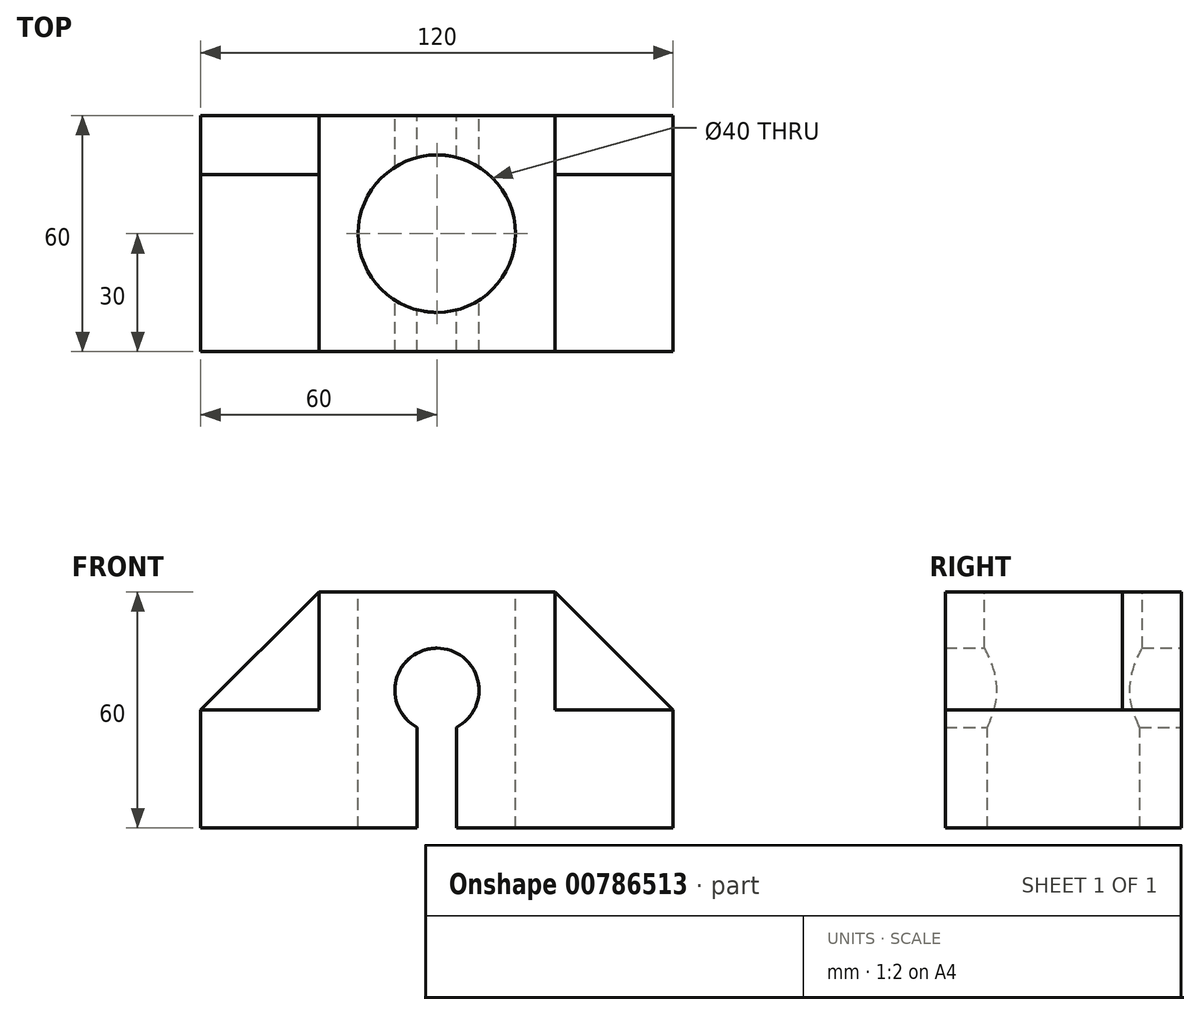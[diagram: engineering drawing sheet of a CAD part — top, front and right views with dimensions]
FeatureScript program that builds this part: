
annotation { "Feature Type Name" : "Feature", "Feature Type Description" : "" }
export const myFeature = defineFeature(function(context is Context, id is Id, definition is map)
    precondition{}
    {
        {
            var Q0;
            Q0=qCreatedBy(makeId("Front.planeOp"),FACE);
            var sketch = newSketch(context, id + "F0", { "sketchPlane" : qUnion([Q0])});
            skLineSegment(sketch, "E0.bottom", {"start": v(-60, 30) * mm, "end": v(60, 30) * mm});
            skLineSegment(sketch, "E0.top", {"start": v(-60, -30) * mm, "end": v(-5, -30) * mm});
            skLineSegment(sketch, "E0.left", {"start": v(-60, 30) * mm, "end": v(-60, -30) * mm});
            skLineSegment(sketch, "E0.right", {"start": v(60, 30) * mm, "end": v(60, -30) * mm});
            skPoint(sketch, "E0.middle", {"position": v(0, 0) * mm});
            skArc(sketch, "E1", {"start": v(5, -4.43) * mm, "mid": v(0, 15.68) * mm, "end": v(-5, -4.43) * mm});
            skLineSegment(sketch, "E2.left", {"start": v(-5, -4.43) * mm, "end": v(-5, -30) * mm});
            skLineSegment(sketch, "E2.right", {"start": v(5, -4.43) * mm, "end": v(5, -30) * mm});
            skPoint(sketch, "E2.middle", {"position": v(0, -30) * mm});
            skPoint(sketch, "E3.orphan", {"position": v(-5, 5) * mm});
            skPoint(sketch, "E4.orphan", {"position": v(5, 5) * mm});
            skPoint(sketch, "E2.top.end.orphan", {"position": v(5, -65) * mm});
            skPoint(sketch, "E2.top.start.orphan", {"position": v(-5, -65) * mm});
            skLineSegment(sketch, "E5.trimOffspring", {"start": v(5, -30) * mm, "end": v(60, -30) * mm});
            skSolve(sketch);
        }
        {
            var Q0;
            Q0=makeQuery(id+"F0.imprint","IMPRINT",FACE,{"disambiguationData":[TD([[makeQuery(id+"F0.imprint","IMPRINT",EDGE,{"derivedFrom":sQuery(id+"F0.wireOp",EDGE,"E0.bottom")}),-1.0]])]});
            extrude(context, id + "F1", {"entities" : qUnion([Q0]), "depth" : 60 * mm, "offsetDistance" : 25 * mm});
        }
        {
            var Q0;
            Q0=makeQuery(id+"F1.opExtrude","CAP_FACE",FACE,{"disambiguationData":[OSD([sQuery(id+"F0.wireOp",EDGE,"E0.bottom"),sQuery(id+"F0.wireOp",EDGE,"E0.top"),sQuery(id+"F0.wireOp",EDGE,"E0.left"),sQuery(id+"F0.wireOp",EDGE,"E0.right"),sQuery(id+"F0.wireOp",EDGE,"E1"),sQuery(id+"F0.wireOp",EDGE,"E2.left"),sQuery(id+"F0.wireOp",EDGE,"E2.right"),sQuery(id+"F0.wireOp",EDGE,"E5.trimOffspring")])],"isStart":false});
            var sketch = newSketch(context, id + "F2", { "sketchPlane" : qUnion([Q0])});
            skLineSegment(sketch, "E6.bottom", {"start": v(60, 0) * mm, "end": v(30, 0) * mm});
            skLineSegment(sketch, "E6.left", {"start": v(60, 0) * mm, "end": v(60, 30) * mm});
            skLineSegment(sketch, "E6.right", {"start": v(30, 0) * mm, "end": v(30, 30) * mm});
            skPoint(sketch, "E6.middle", {"position": v(45, 30) * mm});
            skLineSegment(sketch, "E7", {"start": v(30, 30) * mm, "end": v(60, 30) * mm});
            skPoint(sketch, "E6.top.end.orphan", {"position": v(30, 60) * mm});
            skPoint(sketch, "E8.orphan", {"position": v(60, 60) * mm});
            skLineSegment(sketch, "E9.bottom", {"start": v(-60, 0) * mm, "end": v(-30, 0) * mm});
            skLineSegment(sketch, "E9.left", {"start": v(-60, 0) * mm, "end": v(-60, 30) * mm});
            skLineSegment(sketch, "E9.right", {"start": v(-30, 0) * mm, "end": v(-30, 30) * mm});
            skPoint(sketch, "E9.middle", {"position": v(-45, 30) * mm});
            skLineSegment(sketch, "E10", {"start": v(-30, 30) * mm, "end": v(-60, 30) * mm});
            skPoint(sketch, "E9.top.end.orphan", {"position": v(-30, 60) * mm});
            skPoint(sketch, "E11.orphan", {"position": v(-60, 60) * mm});
            skSolve(sketch);
        }
        {
            var Q0;
            Q0=makeQuery(id+"F2.imprint","IMPRINT",FACE,{"disambiguationData":[TD([[makeQuery(id+"F2.imprint","IMPRINT",EDGE,{"derivedFrom":sQuery(id+"F2.wireOp",EDGE,"E9.bottom")}),1.0]])]});
            var Q1;
            Q1=makeQuery(id+"F2.imprint","IMPRINT",FACE,{"disambiguationData":[TD([[makeQuery(id+"F2.imprint","IMPRINT",EDGE,{"derivedFrom":sQuery(id+"F2.wireOp",EDGE,"E6.bottom")}),-1.0]])]});
            extrude(context, id + "F3", {"entities" : qUnion([Q0, Q1]), "operationType" : NewBodyOperationType.REMOVE, "oppositeDirection" : true, "depth" : 45 * mm, "offsetDistance" : 25 * mm});
        }
        {
            var Q0;
            Q0=makeQuery(id+"F3.boolean.opBoolean","COPY",FACE,{"derivedFrom":makeQuery(id+"F3.opExtrude","CAP_FACE",FACE,{"disambiguationData":[OSD([sQuery(id+"F2.wireOp",EDGE,"E9.bottom"),sQuery(id+"F2.wireOp",EDGE,"E9.left"),sQuery(id+"F2.wireOp",EDGE,"E9.right"),sQuery(id+"F2.wireOp",EDGE,"E10")])],"isStart":false})});
            var sketch = newSketch(context, id + "F4", { "sketchPlane" : qUnion([Q0])});
            skLineSegment(sketch, "E12", {"start": v(-30, 30) * mm, "end": v(-60, 0) * mm});
            skSolve(sketch);
        }
        {
            var Q0;
            Q0=makeQuery(id+"F4.imprint","IMPRINT",FACE,{"disambiguationData":[TD([[makeQuery(id+"F4.imprint","IMPRINT",EDGE,{"derivedFrom":sQuery(id+"F4.wireOp",EDGE,"E12")}),-1.0]])]});
            extrude(context, id + "F5", {"entities" : qUnion([Q0]), "operationType" : NewBodyOperationType.REMOVE, "endBound" : BoundingType.THROUGH_ALL, "oppositeDirection" : true, "depth" : 25 * mm, "offsetDistance" : 25 * mm});
        }
        {
            var Q0;
            Q0=makeQuery(id+"F3.boolean.opBoolean","COPY",FACE,{"derivedFrom":makeQuery(id+"F3.opExtrude","CAP_FACE",FACE,{"disambiguationData":[OSD([sQuery(id+"F2.wireOp",EDGE,"E6.bottom"),sQuery(id+"F2.wireOp",EDGE,"E6.left"),sQuery(id+"F2.wireOp",EDGE,"E6.right"),sQuery(id+"F2.wireOp",EDGE,"E7")])],"isStart":false})});
            var sketch = newSketch(context, id + "F6", { "sketchPlane" : qUnion([Q0])});
            skLineSegment(sketch, "E13", {"start": v(30, 30) * mm, "end": v(60, 0) * mm});
            skSolve(sketch);
        }
        {
            var Q0;
            Q0=makeQuery(id+"F6.imprint","IMPRINT",FACE,{"disambiguationData":[TD([[makeQuery(id+"F6.imprint","IMPRINT",EDGE,{"derivedFrom":sQuery(id+"F6.wireOp",EDGE,"E13")}),1.0]])]});
            extrude(context, id + "F7", {"entities" : qUnion([Q0]), "operationType" : NewBodyOperationType.REMOVE, "endBound" : BoundingType.THROUGH_ALL, "oppositeDirection" : true, "depth" : 25 * mm, "offsetDistance" : 25 * mm});
        }
        {
            var Q0;
            Q0=makeQuery(id+"F1.opExtrude","SWEPT_FACE",FACE,{"disambiguationData":[OSD([sQuery(id+"F0.wireOp",EDGE,"E0.bottom")])]});
            var sketch = newSketch(context, id + "F8", { "sketchPlane" : qUnion([Q0])});
            skCircle(sketch, "E14", {"center": v(0, -30) * mm, "radius": 20 * mm});
            skSolve(sketch);
        }
        {
            var Q0;
            Q0=makeQuery(id+"F8.imprint","IMPRINT",FACE,{"disambiguationData":[TD([[makeQuery(id+"F8.imprint","IMPRINT",EDGE,{"derivedFrom":sQuery(id+"F8.wireOp",EDGE,"E14")}),1.0]])]});
            extrude(context, id + "F9", {"entities" : qUnion([Q0]), "operationType" : NewBodyOperationType.REMOVE, "endBound" : BoundingType.THROUGH_ALL, "oppositeDirection" : true, "depth" : 25 * mm, "offsetDistance" : 25 * mm});
        }
    });
